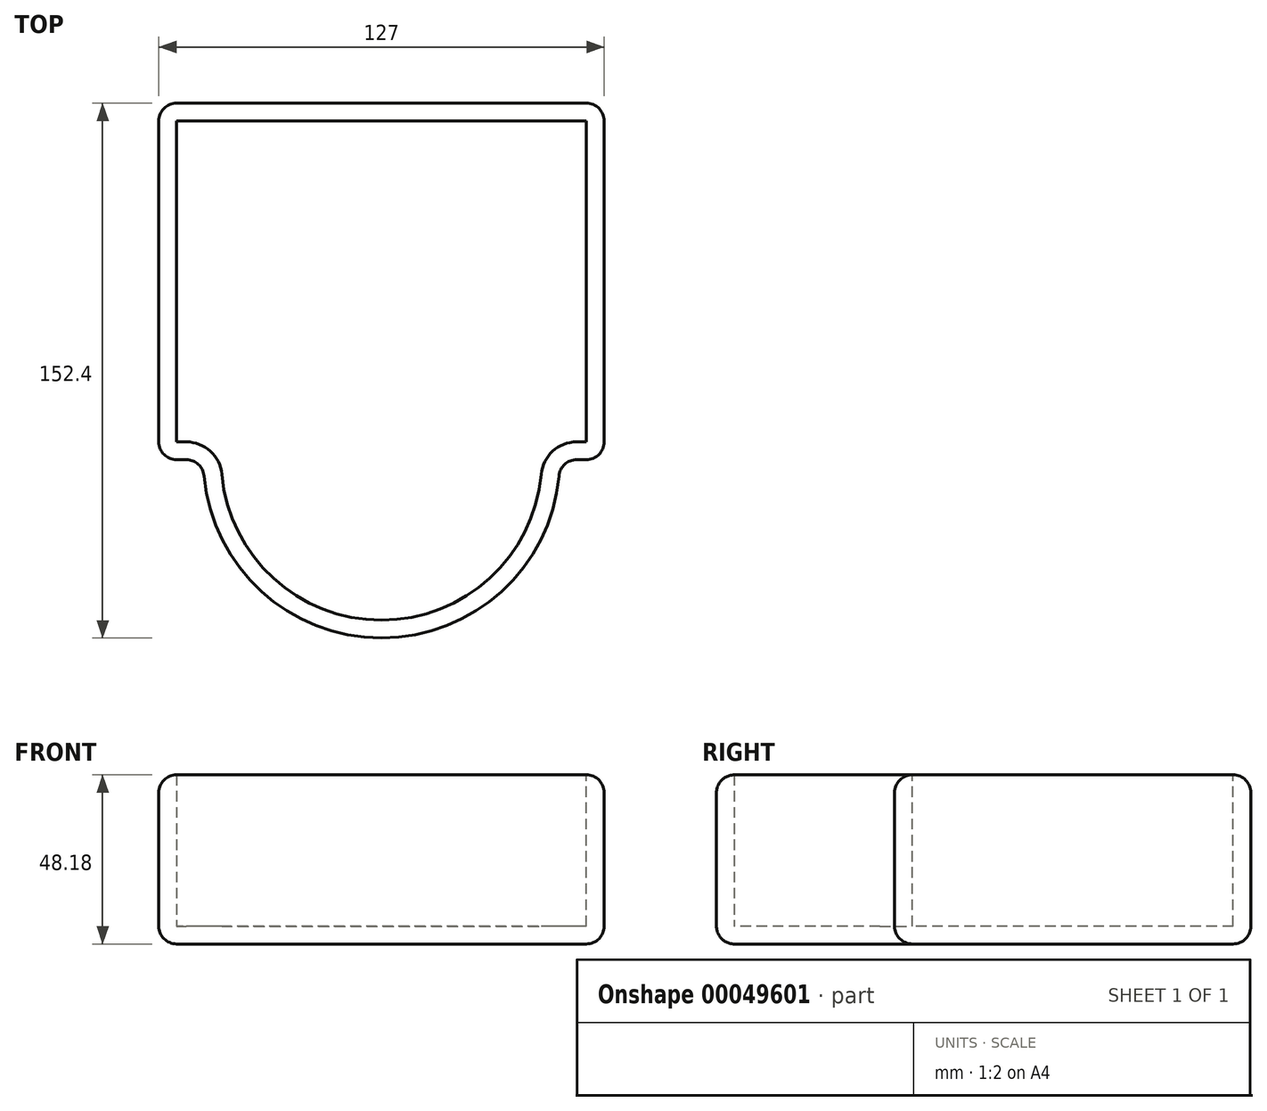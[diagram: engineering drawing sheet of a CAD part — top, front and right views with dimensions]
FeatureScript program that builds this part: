
annotation { "Feature Type Name" : "Feature", "Feature Type Description" : "" }
export const myFeature = defineFeature(function(context is Context, id is Id, definition is map)
    precondition{}
    {
        {
            var Q0;
            Q0=qCreatedBy(makeId("Top.planeOp"),FACE);
            var sketch = newSketch(context, id + "F0", { "sketchPlane" : qUnion([Q0])});
            skLineSegment(sketch, "E0", {"start": v(0, 0) * mm, "end": v(-127, 0) * mm});
            skLineSegment(sketch, "E1", {"start": v(-127, 0) * mm, "end": v(-127, -101.6) * mm});
            skLineSegment(sketch, "E2", {"start": v(-127, -101.6) * mm, "end": v(0, -101.6) * mm});
            skLineSegment(sketch, "E3", {"start": v(0, -101.6) * mm, "end": v(0, 0) * mm});
            skArc(sketch, "E4", {"start": v(-114.3, -101.6) * mm, "mid": v(-63.5, -152.4) * mm, "end": v(-12.7, -101.6) * mm});
            skSolve(sketch);
        }
        {
            var Q0;
            {var subQ0=sQuery(id+"F0.wireOp",EDGE,"E4");Q0=makeQuery(id+"F0.imprint","IMPRINT",FACE,{"disambiguationData":[TD([[makeQuery(id+"F0.imprint","IMPRINT",EDGE,{"derivedFrom":subQ0}),1.0]])]});}
            var Q1;
            Q1=makeQuery(id+"F0.imprint","IMPRINT",FACE,{"disambiguationData":[TD([[makeQuery(id+"F0.imprint","IMPRINT",EDGE,{"derivedFrom":sQuery(id+"F0.wireOp",EDGE,"E0")}),1.0]])]});
            extrude(context, id + "F1", {"entities" : qUnion([Q0, Q1]), "depth" : 48.18 * mm});
        }
        {
            var Q0;
            {var subQ0=sQuery(id+"F0.wireOp",EDGE,"E2");var subQ1=sQuery(id+"F0.wireOp",EDGE,"E4");Q0=makeQuery(id+"F1.opExtrude","SWEPT_EDGE",EDGE,{"disambiguationData":[OSD([subQ0,subQ1]),TDD([makeQuery(id+"F0.imprint","INTERSECT",VERTEX,{"disambiguationData":[OD(0.0)],"derivedFrom":[subQ0,subQ1]})])]});}
            var Q1;
            {var subQ0=sQuery(id+"F0.wireOp",EDGE,"E2");var subQ1=sQuery(id+"F0.wireOp",EDGE,"E4");Q1=makeQuery(id+"F1.opExtrude","SWEPT_EDGE",EDGE,{"disambiguationData":[OSD([subQ0,subQ1]),TDD([makeQuery(id+"F0.imprint","INTERSECT",VERTEX,{"disambiguationData":[OD(1.0)],"derivedFrom":[subQ0,subQ1]})])]});}
            fillet(context, id + "F2", {"entities" : qUnion([Q0, Q1]), "radius" : 5.08 * mm, "tangentPropagation" : true, "allowEdgeOverflow" : false});
        }
        {
            var Q0;
            Q0=makeQuery(id+"F1.opExtrude","CAP_EDGE",EDGE,{"disambiguationData":[OSD([sQuery(id+"F0.wireOp",EDGE,"E1")])],"isStart":false});
            var Q1;
            {var subQ0=sQuery(id+"F0.wireOp",EDGE,"E2");Q1=makeQuery(id+"F1.opExtrude","CAP_EDGE",EDGE,{"disambiguationData":[OSD([subQ0]),TDD([makeQuery(id+"F0.imprint","IMPRINT",EDGE,{"disambiguationData":[TD([[makeQuery(id+"F0.imprint","INTERSECT",VERTEX,{"derivedFrom":[sQuery(id+"F0.wireOp",EDGE,"E1"),subQ0]}),-1.0]])],"derivedFrom":subQ0})])],"isStart":false});}
            var Q2;
            Q2=makeQuery(id+"F1.opExtrude","CAP_EDGE",EDGE,{"disambiguationData":[OSD([sQuery(id+"F0.wireOp",EDGE,"E1")])],"isStart":true});
            var Q3;
            Q3=makeQuery(id+"F1.opExtrude","SWEPT_EDGE",EDGE,{"disambiguationData":[OSD([sQuery(id+"F0.wireOp",EDGE,"E0"),sQuery(id+"F0.wireOp",EDGE,"E1")])]});
            var Q4;
            Q4=makeQuery(id+"F1.opExtrude","CAP_EDGE",EDGE,{"disambiguationData":[OSD([sQuery(id+"F0.wireOp",EDGE,"E4")])],"isStart":false});
            var Q5;
            Q5=makeQuery(id+"F1.opExtrude","CAP_EDGE",EDGE,{"disambiguationData":[OSD([sQuery(id+"F0.wireOp",EDGE,"E0")])],"isStart":false});
            var Q6;
            Q6=makeQuery(id+"F1.opExtrude","CAP_EDGE",EDGE,{"disambiguationData":[OSD([sQuery(id+"F0.wireOp",EDGE,"E3")])],"isStart":false});
            var Q7;
            {var subQ0=sQuery(id+"F0.wireOp",EDGE,"E2");Q7=makeQuery(id+"F1.opExtrude","CAP_EDGE",EDGE,{"disambiguationData":[OSD([subQ0]),TDD([makeQuery(id+"F0.imprint","IMPRINT",EDGE,{"disambiguationData":[TD([[makeQuery(id+"F0.imprint","INTERSECT",VERTEX,{"derivedFrom":[subQ0,sQuery(id+"F0.wireOp",EDGE,"E3")]}),1.0]])],"derivedFrom":subQ0})])],"isStart":false});}
            var Q8;
            Q8=makeQuery(id+"F1.opExtrude","SWEPT_EDGE",EDGE,{"disambiguationData":[OSD([sQuery(id+"F0.wireOp",EDGE,"E1"),sQuery(id+"F0.wireOp",EDGE,"E2")])]});
            var Q9;
            {var subQ0=sQuery(id+"F0.wireOp",EDGE,"E2");Q9=makeQuery(id+"F1.opExtrude","CAP_EDGE",EDGE,{"disambiguationData":[OSD([subQ0]),TDD([makeQuery(id+"F0.imprint","IMPRINT",EDGE,{"disambiguationData":[TD([[makeQuery(id+"F0.imprint","INTERSECT",VERTEX,{"derivedFrom":[sQuery(id+"F0.wireOp",EDGE,"E1"),subQ0]}),-1.0]])],"derivedFrom":subQ0})])],"isStart":true});}
            var Q10;
            Q10=makeQuery(id+"F1.opExtrude","CAP_EDGE",EDGE,{"disambiguationData":[OSD([sQuery(id+"F0.wireOp",EDGE,"E4")])],"isStart":true});
            var Q11;
            {var subQ0=sQuery(id+"F0.wireOp",EDGE,"E2");Q11=makeQuery(id+"F1.opExtrude","CAP_EDGE",EDGE,{"disambiguationData":[OSD([subQ0]),TDD([makeQuery(id+"F0.imprint","IMPRINT",EDGE,{"disambiguationData":[TD([[makeQuery(id+"F0.imprint","INTERSECT",VERTEX,{"derivedFrom":[subQ0,sQuery(id+"F0.wireOp",EDGE,"E3")]}),1.0]])],"derivedFrom":subQ0})])],"isStart":true});}
            var Q12;
            Q12=makeQuery(id+"F1.opExtrude","CAP_EDGE",EDGE,{"disambiguationData":[OSD([sQuery(id+"F0.wireOp",EDGE,"E0")])],"isStart":true});
            var Q13;
            Q13=makeQuery(id+"F1.opExtrude","SWEPT_EDGE",EDGE,{"disambiguationData":[OSD([sQuery(id+"F0.wireOp",EDGE,"E2"),sQuery(id+"F0.wireOp",EDGE,"E3")])]});
            var Q14;
            Q14=makeQuery(id+"F1.opExtrude","CAP_FACE",FACE,{"disambiguationData":[OSD([sQuery(id+"F0.wireOp",EDGE,"E0"),sQuery(id+"F0.wireOp",EDGE,"E1"),sQuery(id+"F0.wireOp",EDGE,"E2"),sQuery(id+"F0.wireOp",EDGE,"E3"),sQuery(id+"F0.wireOp",EDGE,"E4")])],"isStart":true});
            var Q15;
            Q15=makeQuery(id+"F1.opExtrude","CAP_EDGE",EDGE,{"disambiguationData":[OSD([sQuery(id+"F0.wireOp",EDGE,"E3")])],"isStart":true});
            var Q16;
            Q16=makeQuery(id+"F1.opExtrude","SWEPT_EDGE",EDGE,{"disambiguationData":[OSD([sQuery(id+"F0.wireOp",EDGE,"E0"),sQuery(id+"F0.wireOp",EDGE,"E3")])]});
            fillet(context, id + "F3", {"entities" : qUnion([Q0, Q1, Q2, Q3, Q4, Q5, Q6, Q7, Q8, Q9, Q10, Q11, Q12, Q13, Q14, Q15, Q16]), "radius" : 5.08 * mm, "tangentPropagation" : true, "allowEdgeOverflow" : false});
        }
        {
            var Q0;
            Q0=makeQuery(id+"F1.opExtrude","CAP_FACE",FACE,{"disambiguationData":[OSD([sQuery(id+"F0.wireOp",EDGE,"E0"),sQuery(id+"F0.wireOp",EDGE,"E1"),sQuery(id+"F0.wireOp",EDGE,"E2"),sQuery(id+"F0.wireOp",EDGE,"E3"),sQuery(id+"F0.wireOp",EDGE,"E4")])],"isStart":false});
            shell(context, id + "F4", {"entities" : qUnion([Q0]), "thickness" : 5.08 * mm});
        }
    });
